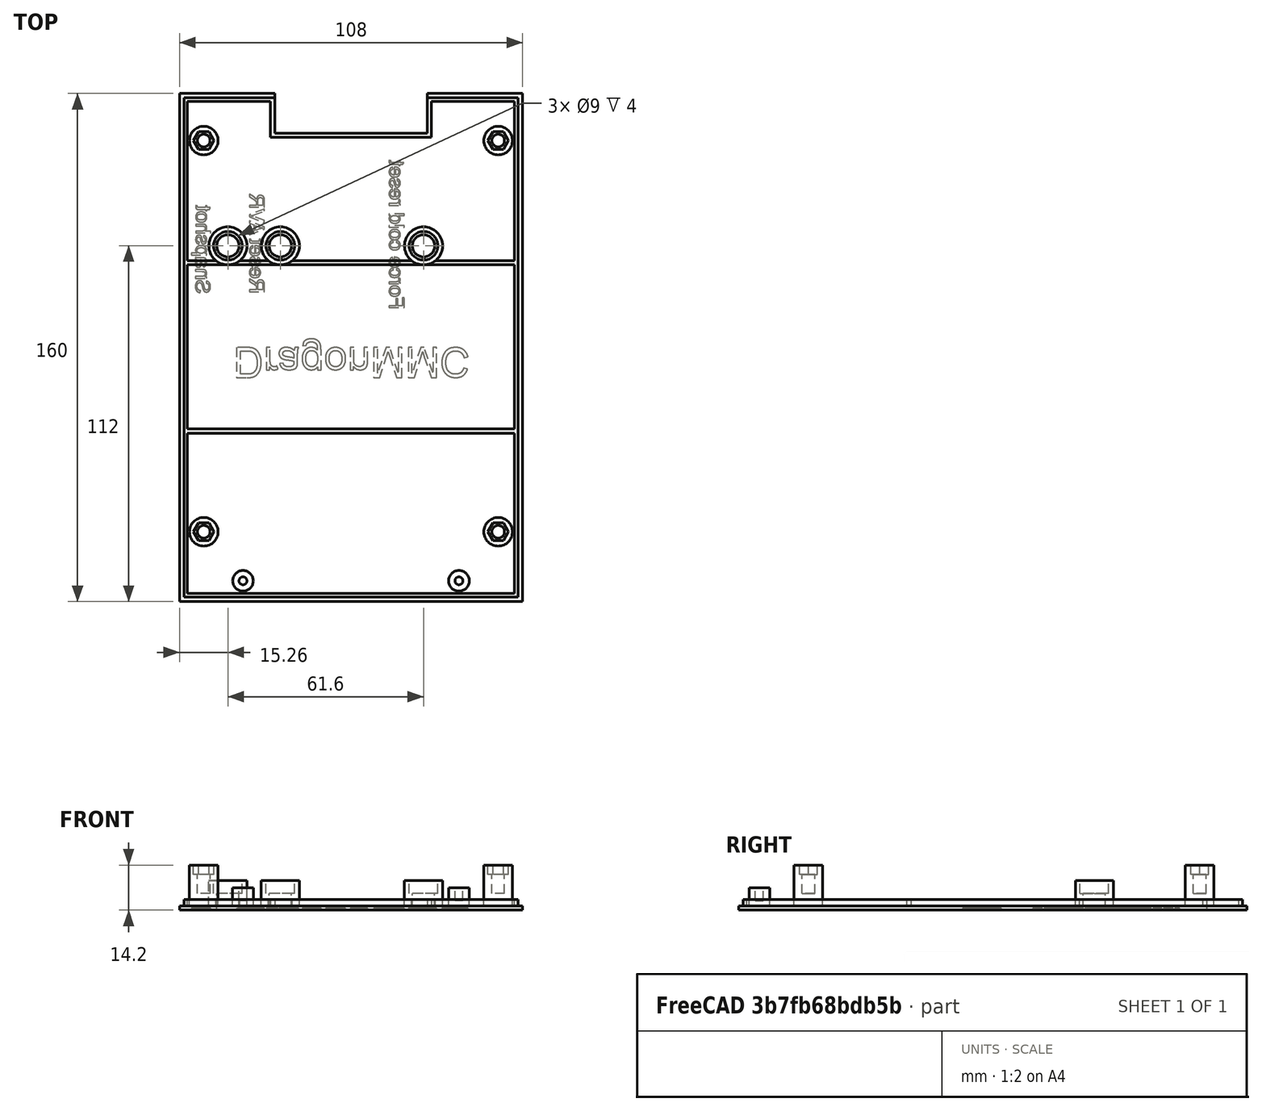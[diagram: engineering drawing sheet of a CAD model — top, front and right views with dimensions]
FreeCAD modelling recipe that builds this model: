
FCSTD DOCUMENT  (FreeCAD 0.18R4 (GitTag))
Label: DragonMMCTop-v5
License: All rights reserved
LicenseURL: http://en.wikipedia.org/wiki/All_rights_reserved
objects: Part::Cylinder×9, Part::Box×8, Part::Cut×8, Part::MultiFuse×6, Part::FeaturePython×6, Part::Extrusion×5, Part::Part2DObjectPython×4, Part::RegularPolygon×1
note: 47 computed .brp shape members not serialized (recipe doc carries the construction recipe); baked Part::Feature solids carry a one-line shape summary decoded from their .brp

FEATURE [Part::Box] Box  label="Top plate"
  AttacherType = Attacher::AttachEngine3D
  Height = 1.3
  Length = 108
  Width = 160
FEATURE [Part::Box] Box002  label="Cube002"
  AttacherType = Attacher::AttachEngine3D
  Height = 2
  Length = 103
  Placement = pos=(2.5,2.5,1.3) rot=(0,0,1;0rad)
  Width = 155
FEATURE [Part::Box] Box001  label="Cube001"
  AttacherType = Attacher::AttachEngine3D
  Height = 3.3
  Length = 105.2
  Placement = pos=(1.4,1.4,0) rot=(0,0,1;0rad)
  Width = 157.2
FEATURE [Part::Cut] Cut  label="Border wall"
  Base = -> Box001
  Tool = -> Box002
FEATURE [Part::MultiFuse] Fusion  label="Top plate plus wall"
  Shapes = -> [Box,Cut]
FEATURE [Part::Cylinder] Cylinder
  Angle = 360
  AttacherType = Attacher::AttachEngine3D
  Height = 7
  Placement = pos=(20,6.5,0) rot=(0,0,1;0rad)
  Radius = 3.25
FEATURE [Part::Cylinder] Cylinder001
  Angle = 360
  AttacherType = Attacher::AttachEngine3D
  Height = 4
  Placement = pos=(20,6.5,3) rot=(0,0,1;0rad)
  Radius = 1.25
FEATURE [Part::Cut] Cut002  label="Left support"
  Base = -> Cylinder
  Tool = -> Cylinder001
FEATURE [Part::FeaturePython] Clone  label="Right Support"  # Draft clone (typed FeaturePython)
  AttacherType = Attacher::AttachEngine3D
  Fuse = false
  Objects = -> [Cut002]
  Placement = pos=(68,0,0) rot=(0,0,1;0rad)
  Scale = (1,1,1)
FEATURE [Part::Box] Box007  label="Card access cutout"
  AttacherType = Attacher::AttachEngine3D
  Height = 3.3
  Length = 48
  Placement = pos=(30,147.5,0) rot=(0,0,1;0rad)
  Width = 12.5
FEATURE [Part::Cut] Cut003  label="Top plus wall and card cutout"
  Base = -> Fusion
  Tool = -> Box007
FEATURE [Part::Cylinder] Cylinder002  label="Board Post 1"
  Angle = 360
  AttacherType = Attacher::AttachEngine3D
  Height = 14.2
  Placement = pos=(7.65,145.14,0) rot=(0,0,1;0rad)
  Radius = 4.5
FEATURE [Part::Cylinder] Cylinder003  label="Board Post 1 drill"
  Angle = 360
  AttacherType = Attacher::AttachEngine3D
  Height = 9
  Placement = pos=(7.65,145.14,5.2) rot=(0,0,1;0rad)
  Radius = 2
FEATURE [Part::Cut] Cut004  label="Board post 1 and drill"
  Base = -> Cylinder002
  Tool = -> Cylinder003
FEATURE [Part::Cylinder] Cylinder004  label="Switch appature 1"
  Angle = 360
  AttacherType = Attacher::AttachEngine3D
  Height = 9.3
  Placement = pos=(15.26,112,0) rot=(0,0,1;0rad)
  Radius = 6
FEATURE [Part::Cylinder] Cylinder005  label="Switch appature 2"
  Angle = 360
  AttacherType = Attacher::AttachEngine3D
  Height = 9.3
  Placement = pos=(31.77,112,0) rot=(0,0,1;0rad)
  Radius = 6
FEATURE [Part::Cylinder] Cylinder006  label="Switch appature 3"
  Angle = 360
  AttacherType = Attacher::AttachEngine3D
  Height = 9.3
  Placement = pos=(76.86,112,0) rot=(0,0,1;0rad)
  Radius = 6
FEATURE [Part::Cylinder] Cylinder007  label="Switch appature inner drill 1"
  Angle = 360
  AttacherType = Attacher::AttachEngine3D
  Height = 4
  Placement = pos=(15.26,112,5.3) rot=(0,0,1;0rad)
  Radius = 4.5
FEATURE [Part::Box] Box008  label="Cube"
  AttacherType = Attacher::AttachEngine3D
  Height = 2
  Length = 50.6
  Placement = pos=(28.7,146.2,1.3) rot=(0,0,1;0rad)
  Width = 12.4
FEATURE [Part::Box] Box009  label="Cube003"
  AttacherType = Attacher::AttachEngine3D
  Height = 2
  Length = 48
  Placement = pos=(30,147.5,1.3) rot=(0,0,1;0rad)
  Width = 11.1
FEATURE [Part::Cut] Cut006  label="Cutout wall"
  Base = -> Box008
  Tool = -> Box009
FEATURE [Part::Cylinder] Cylinder008  label="Switch appature outer drill 1"
  Angle = 360
  AttacherType = Attacher::AttachEngine3D
  Height = 5.3
  Placement = pos=(15.26,112,0) rot=(0,0,1;0rad)
  Radius = 3.5
FEATURE [Part::MultiFuse] Fusion001  label="Switch appature drills 1"
  Shapes = -> [Cylinder007,Cylinder008]
FEATURE [Part::MultiFuse] Fusion002  label="Top walls and switch apatures"
  Shapes = -> [Cylinder004,Cylinder006,Cylinder005,Cut003]
FEATURE [Part::FeaturePython] Clone004  label="Switch appature drills 2"  # Draft clone (typed FeaturePython)
  AttacherType = Attacher::AttachEngine3D
  Fuse = false
  Objects = -> [Fusion001]
  Placement = pos=(16.51,0,0) rot=(0,0,1;0rad)
  Scale = (1,1,1)
FEATURE [Part::FeaturePython] Clone005  label="Switch appature drills 3"  # Draft clone (typed FeaturePython)
  AttacherType = Attacher::AttachEngine3D
  Fuse = false
  Objects = -> [Fusion001]
  Placement = pos=(61.6,0,0) rot=(0,0,1;0rad)
  Scale = (1,1,1)
FEATURE [Part::MultiFuse] Fusion003  label="All switch drills"
  Shapes = -> [Fusion001,Clone004,Clone005]
FEATURE [Part::Cut] Cut007  label="Top walls and switches drilled"
  Base = -> Fusion002
  Tool = -> Fusion003
FEATURE [Part::RegularPolygon] RegularPolygon  label="Regular polygon"
  AttacherType = Attacher::AttachEngine3D
  Circumradius = 3.25
  Polygon = 6
FEATURE [Part::Extrusion] Extrude  label="M3 nut cutout"
  Base = -> RegularPolygon
  Dir = (0,0,1)
  DirMode = 0
  FaceMakerClass = Part::FaceMakerBullseye
  LengthFwd = 3
  LengthRev = 0
  Placement = pos=(7.65,145.14,11.2) rot=(0,0,1;0rad)
  Solid = true
  Symmetric = false
FEATURE [Part::Cut] Cut008  label="Board post 1 drill and nut"
  Base = -> Cut004
  Tool = -> Extrude
FEATURE [Part::FeaturePython] Clone006  label="Board post 2 drill and nut"  # Draft clone (typed FeaturePython)
  AttacherType = Attacher::AttachEngine3D
  Fuse = false
  Objects = -> [Cut008]
  Placement = pos=(92.7,0,0) rot=(0,0,1;0rad)
  Scale = (1,1,1)
FEATURE [Part::FeaturePython] Clone007  label="Board post 3 drill and nut"  # Draft clone (typed FeaturePython)
  AttacherType = Attacher::AttachEngine3D
  Fuse = false
  Objects = -> [Cut008]
  Placement = pos=(0,-123.19,0) rot=(0,0,1;0rad)
  Scale = (1,1,1)
FEATURE [Part::FeaturePython] Clone008  label="Board post 4 drill and nut"  # Draft clone (typed FeaturePython)
  AttacherType = Attacher::AttachEngine3D
  Fuse = false
  Objects = -> [Cut008]
  Placement = pos=(92.7,-123.19,0) rot=(0,0,1;0rad)
  Scale = (1,1,1)
FEATURE [Part::Part2DObjectPython] ShapeString  # Draft 2D object (typed FeaturePython)
  FontFile = <path>
  Size = 10
  String = DragonMMC
  Tracking = 0
FEATURE [Part::Extrusion] Extrude001  label="Name Text"
  Base = -> ShapeString
  Dir = (0,0,1)
  DirMode = 2
  FaceMakerClass = Part::FaceMakerBullseye
  LengthFwd = 0.5
  LengthRev = 0
  Placement = pos=(17,80,0.5) rot=(1,0,0;3.14159rad)
  Solid = true
  Symmetric = false
FEATURE [Part::Box] Box010  label="Brace 1"
  AttacherType = Attacher::AttachEngine3D
  Height = 2
  Length = 103
  Placement = pos=(2.5,53,1.3) rot=(0,0,1;0rad)
  Width = 1.3
FEATURE [Part::Box] Box011  label="Brace 2"
  AttacherType = Attacher::AttachEngine3D
  Height = 2
  Length = 103
  Placement = pos=(2.5,106,1.3) rot=(0,0,1;0rad)
  Width = 1.3
FEATURE [Part::Part2DObjectPython] ShapeString001  label="ShapeString Snapshot"  # Draft 2D object (typed FeaturePython)
  FontFile = <path>
  Size = 5
  String = Snapshot
  Tracking = 0
FEATURE [Part::Part2DObjectPython] ShapeString002  label="ShapeString ResetAVR"  # Draft 2D object (typed FeaturePython)
  FontFile = <path>
  Size = 5
  String = Reset AVR
  Tracking = 0
FEATURE [Part::Part2DObjectPython] ShapeString003  label="ShapeString Force cold"  # Draft 2D object (typed FeaturePython)
  FontFile = <path>
  Size = 5
  String = Force cold reset
  Tracking = 0
FEATURE [Part::Extrusion] Extrude002  label="Snapshot Text"
  Base = -> ShapeString001
  Dir = (0,0,1)
  DirMode = 2
  FaceMakerClass = Part::FaceMakerBullseye
  LengthFwd = 0.5
  LengthRev = 0
  Placement = pos=(5,97,0.5) rot=(0.708549,0.705662,0;3.14159rad)
  Solid = false
  Symmetric = false
FEATURE [Part::Extrusion] Extrude003  label="Reset AVR Text"
  Base = -> ShapeString002
  Dir = (0,0,1)
  DirMode = 2
  FaceMakerClass = Part::FaceMakerBullseye
  LengthFwd = 0.5
  LengthRev = 0
  Placement = pos=(22,97,0.5) rot=(0.707107,0.707107,0;3.14159rad)
  Solid = false
  Symmetric = false
FEATURE [Part::Extrusion] Extrude004  label="Force cold Text"
  Base = -> ShapeString003
  Dir = (0,0,1)
  DirMode = 2
  FaceMakerClass = Part::FaceMakerBullseye
  LengthFwd = 0.5
  LengthRev = 0
  Placement = pos=(66,92,0.5) rot=(0.707107,0.707107,0;3.14159rad)
  Solid = false
  Symmetric = false
FEATURE [Part::MultiFuse] Fusion004  label="All Text"
  Shapes = -> [Extrude002,Extrude003,Extrude004,Extrude001]
FEATURE [Part::Cut] Cut009  label="Top plus all text"
  Base = -> Cut007
  Tool = -> Fusion004
FEATURE [Part::MultiFuse] Fusion005  label="Top plus all elements"
  Shapes = -> [Cut009,Clone006,Clone,Clone008,Clone007,Cut006,Cut002,Cut008,Box011,Box010]
note: 4 file-system paths scrubbed to <path> (originals preserved in the JSON sidecar)
